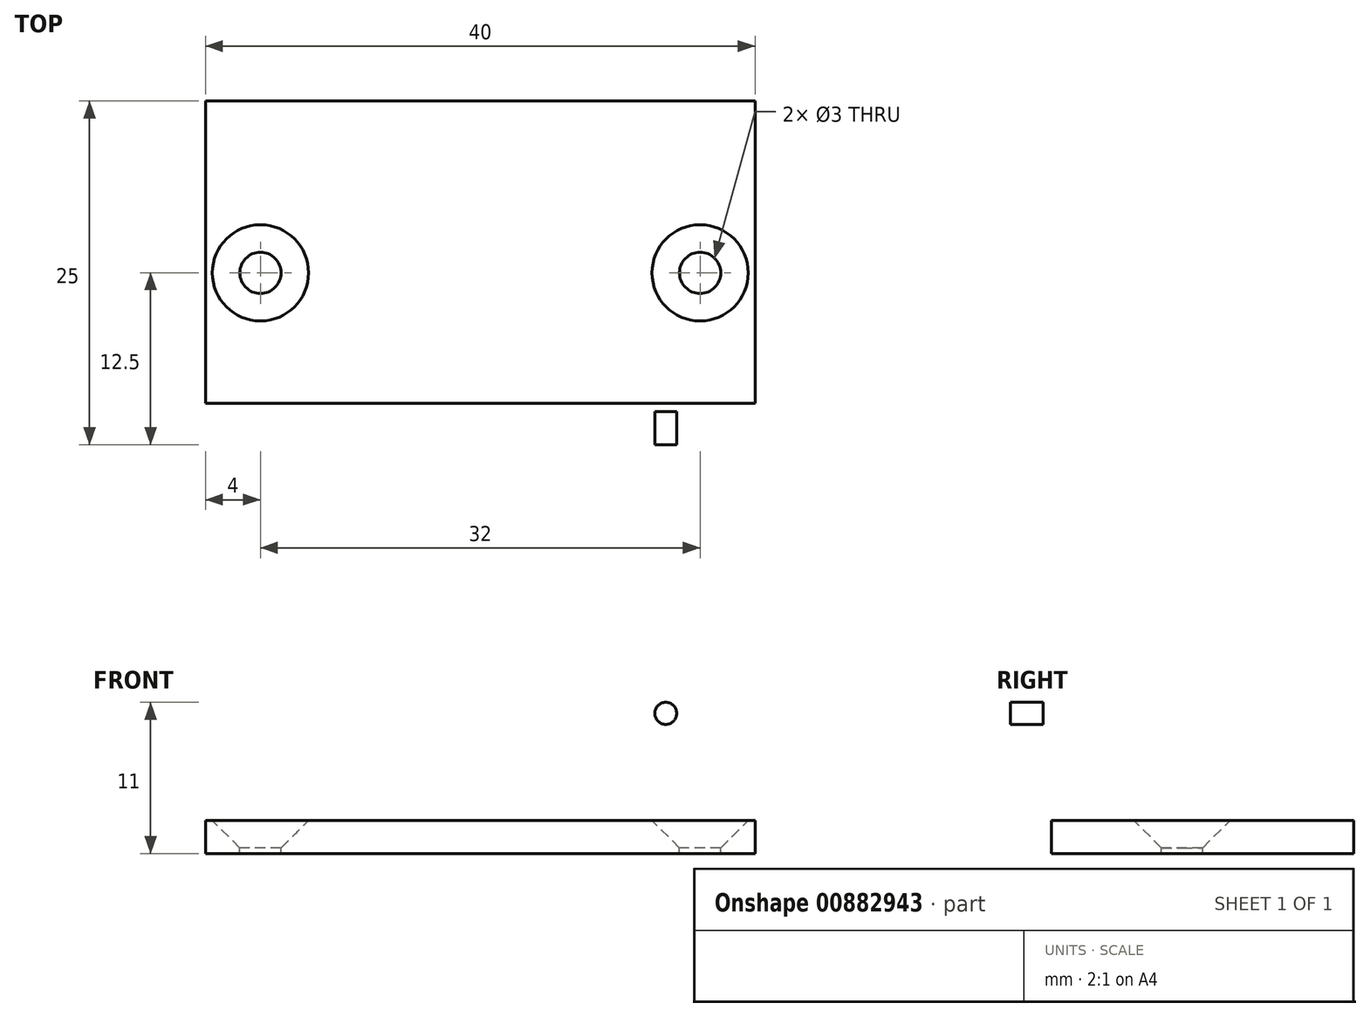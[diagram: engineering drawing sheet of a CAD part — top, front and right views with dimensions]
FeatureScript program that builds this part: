
annotation { "Feature Type Name" : "Feature", "Feature Type Description" : "" }
export const myFeature = defineFeature(function(context is Context, id is Id, definition is map)
    precondition{}
    {
        {
            var Q0;
            Q0=qCreatedBy(makeId("Top.planeOp"),FACE);
            var sketch = newSketch(context, id + "F0", { "sketchPlane" : qUnion([Q0])});
            skLineSegment(sketch, "E0.bottom", {"start": v(20, 12.5) * mm, "end": v(-20, 12.5) * mm});
            skLineSegment(sketch, "E0.top", {"start": v(20, -12.5) * mm, "end": v(-20, -12.5) * mm});
            skLineSegment(sketch, "E0.left", {"start": v(20, 12.5) * mm, "end": v(20, -12.5) * mm});
            skLineSegment(sketch, "E0.right", {"start": v(-20, 12.5) * mm, "end": v(-20, -12.5) * mm});
            skPoint(sketch, "E0.middle", {"position": v(0, 0) * mm});
            skLineSegment(sketch, "E1.bottom", {"start": v(-20, -12.5) * mm, "end": v(20, -12.5) * mm});
            skLineSegment(sketch, "E1.top", {"start": v(-20, -10.1) * mm, "end": v(20, -10.1) * mm});
            skLineSegment(sketch, "E1.left", {"start": v(-20, -12.5) * mm, "end": v(-20, -10.1) * mm});
            skLineSegment(sketch, "E1.right", {"start": v(20, -12.5) * mm, "end": v(20, -10.1) * mm});
            skLineSegment(sketch, "E2", {"start": v(-20, 0) * mm, "end": v(20, 0) * mm, "construction": true});
            skLineSegment(sketch, "E3", {"start": v(20, 0) * mm, "end": v(16, 0) * mm, "construction": true});
            skLineSegment(sketch, "E4", {"start": v(-20, 0) * mm, "end": v(-16, 0) * mm, "construction": true});
            skCircle(sketch, "E5", {"center": v(-16, 0) * mm, "radius": 1.5 * mm});
            skCircle(sketch, "E6", {"center": v(16, 0) * mm, "radius": 1.5 * mm});
            skSolve(sketch);
        }
        {
            var Q0;
            {var subQ0=sQuery(id+"F0.wireOp",EDGE,"E0.top");Q0=makeQuery(id+"F0.imprint","IMPRINT",FACE,{"disambiguationData":[TD([[makeQuery(id+"F0.imprint","IMPRINT",EDGE,{"derivedFrom":subQ0}),-1.0]])]});}
            var Q1;
            {var subQ2=sQuery(id+"F0.wireOp",EDGE,"E0.bottom");Q1=makeQuery(id+"F0.imprint","IMPRINT",FACE,{"disambiguationData":[TD([[makeQuery(id+"F0.imprint","IMPRINT",EDGE,{"derivedFrom":subQ2}),1.0]])]});}
            extrude(context, id + "F1", {"entities" : qUnion([Q0, Q1]), "oppositeDirection" : true, "depth" : 2.4 * mm, "offsetDistance" : 25 * mm});
        }
        {
            var Q0;
            {var subQ0=sQuery(id+"F0.wireOp",EDGE,"E0.top");Q0=makeQuery(id+"F0.imprint","IMPRINT",FACE,{"disambiguationData":[TD([[makeQuery(id+"F0.imprint","IMPRINT",EDGE,{"derivedFrom":subQ0}),-1.0]])]});}
            extrude(context, id + "F2", {"entities" : qUnion([Q0]), "operationType" : NewBodyOperationType.ADD, "depth" : 18 * mm, "offsetDistance" : 25 * mm});
        }
        {
            var Q0;
            {var subQ0=sQuery(id+"F0.wireOp",EDGE,"E0.top");Q0=makeQuery(id+"F2.boolean.opBoolean","MERGE",FACE,{"derivedFrom":[makeQuery(id+"F1.opExtrude","SWEPT_FACE",FACE,{"disambiguationData":[OSD([subQ0])]}),makeQuery(id+"F2.opExtrude","SWEPT_FACE",FACE,{"disambiguationData":[OSD([subQ0])]})]});}
            var sketch = newSketch(context, id + "F3", { "sketchPlane" : qUnion([Q0])});
            skLineSegment(sketch, "E7", {"start": v(0, 0) * mm, "end": v(0, 18) * mm, "construction": true});
            skLineSegment(sketch, "E8", {"start": v(0, 1.55) * mm, "end": v(0, 7.8) * mm, "construction": true});
            skLineSegment(sketch, "E9.bottom", {"start": v(11.38, 1.3) * mm, "end": v(-11.37, 1.3) * mm});
            skLineSegment(sketch, "E9.top", {"start": v(11.38, 14.3) * mm, "end": v(-11.37, 14.3) * mm});
            skLineSegment(sketch, "E9.left", {"start": v(11.38, 1.3) * mm, "end": v(11.38, 14.3) * mm});
            skLineSegment(sketch, "E9.right", {"start": v(-11.37, 1.3) * mm, "end": v(-11.37, 14.3) * mm});
            skPoint(sketch, "E9.middle", {"position": v(0, 7.8) * mm});
            skPoint(sketch, "E10.endSnap0", {"position": v(20, 7.8) * mm});
            skLineSegment(sketch, "E11", {"start": v(0, 7.8) * mm, "end": v(-13.5, 7.8) * mm, "construction": true});
            skCircle(sketch, "E12", {"center": v(-13.5, 7.8) * mm, "radius": 0.8 * mm});
            skCircle(sketch, "E13.MirrorC", {"center": v(13.5, 7.8) * mm, "radius": 0.8 * mm});
            skSolve(sketch);
        }
        {
            var Q0;
            Q0=makeQuery(id+"F3.imprint","IMPRINT",FACE,{"disambiguationData":[TD([[makeQuery(id+"F3.imprint","IMPRINT",EDGE,{"derivedFrom":sQuery(id+"F3.wireOp",EDGE,"E9.bottom")}),-1.0]])]});
            var Q1;
            Q1=makeQuery(id+"F3.imprint","IMPRINT",FACE,{"disambiguationData":[TD([[makeQuery(id+"F3.imprint","IMPRINT",EDGE,{"derivedFrom":sQuery(id+"F3.wireOp",EDGE,"E13.MirrorC")}),-1.0]])]});
            var Q2;
            Q2=makeQuery(id+"F3.imprint","IMPRINT",FACE,{"disambiguationData":[TD([[makeQuery(id+"F3.imprint","IMPRINT",EDGE,{"derivedFrom":sQuery(id+"F3.wireOp",EDGE,"E12")}),1.0]])]});
            extrude(context, id + "F4", {"entities" : qUnion([Q0, Q1, Q2]), "operationType" : NewBodyOperationType.REMOVE, "oppositeDirection" : true, "depth" : 3 * mm, "offsetDistance" : 25 * mm});
        }
        {
            var Q0;
            Q0=makeQuery(id+"F1.opExtrude","CAP_EDGE",EDGE,{"disambiguationData":[OSD([sQuery(id+"F0.wireOp",EDGE,"E5")])],"isStart":true});
            var Q1;
            Q1=makeQuery(id+"F1.opExtrude","CAP_EDGE",EDGE,{"disambiguationData":[OSD([sQuery(id+"F0.wireOp",EDGE,"E6")])],"isStart":true});
            chamfer(context, id + "F5", {"entities" : qUnion([Q0, Q1]), "width" : 2 * mm, "tangentPropagation" : true});
        }
    });
